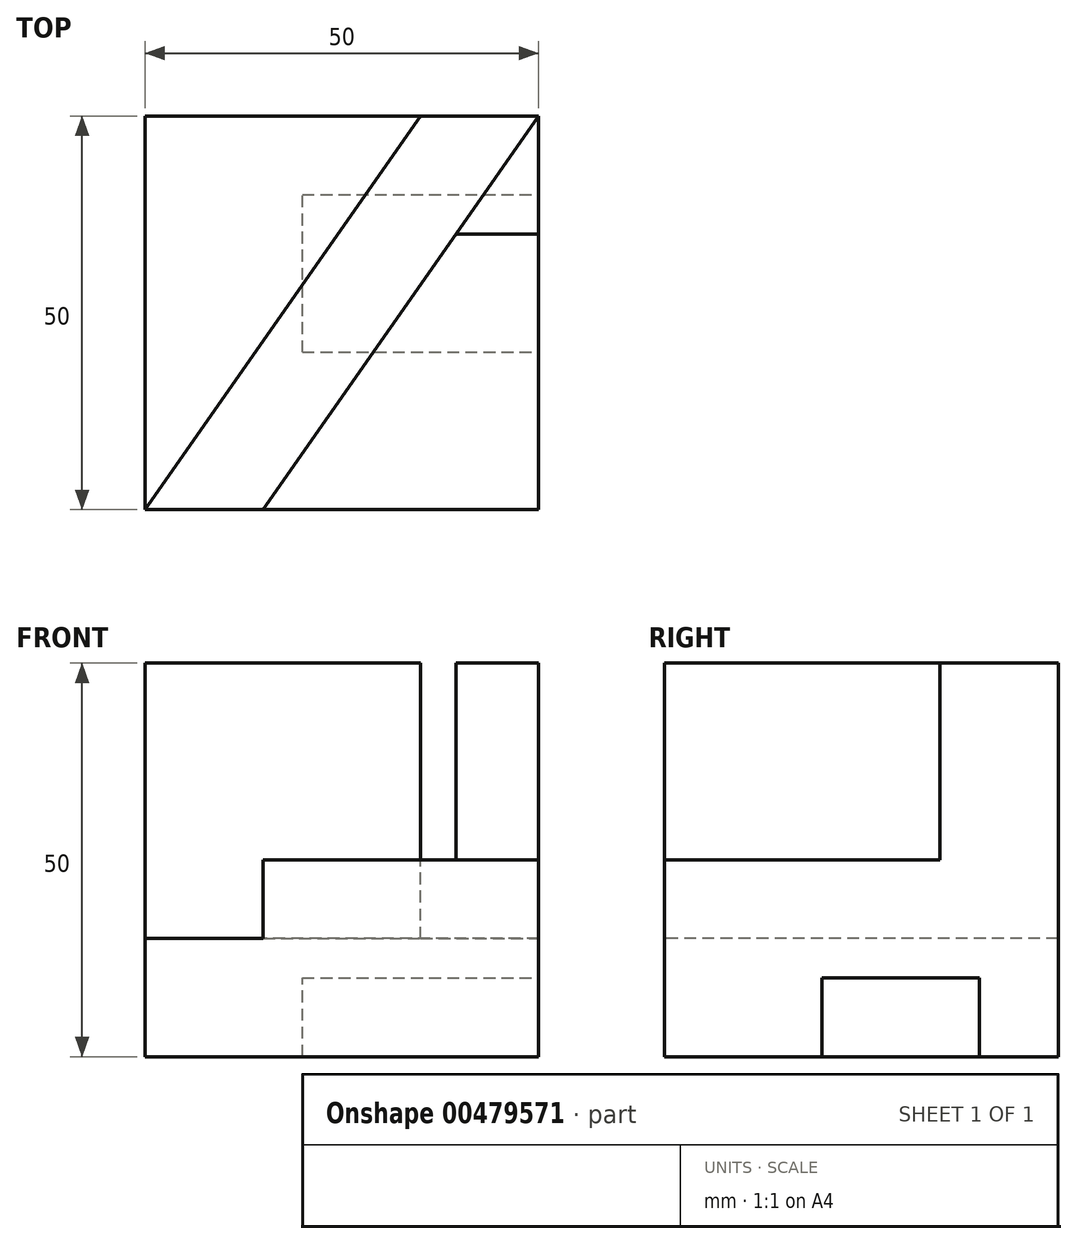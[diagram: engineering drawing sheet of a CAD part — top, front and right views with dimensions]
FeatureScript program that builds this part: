
annotation { "Feature Type Name" : "Feature", "Feature Type Description" : "" }
export const myFeature = defineFeature(function(context is Context, id is Id, definition is map)
    precondition{}
    {
        {
            var Q0;
            Q0=qCreatedBy(makeId("Top.planeOp"),FACE);
            var sketch = newSketch(context, id + "F0", { "sketchPlane" : qUnion([Q0])});
            skLineSegment(sketch, "E0.bottom", {"start": v(0, 0) * mm, "end": v(50, 0) * mm});
            skLineSegment(sketch, "E0.top", {"start": v(0, 50) * mm, "end": v(50, 50) * mm});
            skLineSegment(sketch, "E0.left", {"start": v(0, 0) * mm, "end": v(0, 50) * mm});
            skLineSegment(sketch, "E0.right", {"start": v(50, 0) * mm, "end": v(50, 50) * mm});
            skSolve(sketch);
        }
        {
            var Q0;
            Q0 = qSketchRegion(id + "F0", true);
            extrude(context, id + "F1", {"entities" : qUnion([Q0]), "depth" : 50 * mm});
        }
        {
            var Q0;
            Q0=makeQuery(id+"F1.opExtrude","CAP_FACE",FACE,{"disambiguationData":[OSD([sQuery(id+"F0.wireOp",EDGE,"E0.bottom"),sQuery(id+"F0.wireOp",EDGE,"E0.top"),sQuery(id+"F0.wireOp",EDGE,"E0.left"),sQuery(id+"F0.wireOp",EDGE,"E0.right")])],"isStart":false});
            var sketch = newSketch(context, id + "F2", { "sketchPlane" : qUnion([Q0])});
            skLineSegment(sketch, "E1", {"start": v(50, 50) * mm, "end": v(15, 0) * mm});
            skLineSegment(sketch, "E2", {"start": v(0, 0) * mm, "end": v(35, 50) * mm});
            skSolve(sketch);
        }
        {
            var Q0;
            Q0 = qSketchRegion(id + "F2", true);
            var Q1;
            {var subQ0=sQuery(id+"F2.wireOp",EDGE,"E1");Q1=makeQuery(id+"F2.imprint","IMPRINT",FACE,{"disambiguationData":[TD([[makeQuery(id+"F2.imprint","IMPRINT",EDGE,{"derivedFrom":subQ0}),-1.0]])]});}
            extrude(context, id + "F3", {"entities" : qUnion([Q0, Q1]), "operationType" : NewBodyOperationType.REMOVE, "oppositeDirection" : true, "depth" : 35 * mm});
        }
        {
            var Q0;
            Q0=makeQuery(id+"F1.opExtrude","SWEPT_FACE",FACE,{"disambiguationData":[OSD([sQuery(id+"F0.wireOp",EDGE,"E0.right")])]});
            var sketch = newSketch(context, id + "F4", { "sketchPlane" : qUnion([Q0])});
            skLineSegment(sketch, "E3.bottom", {"start": v(20, 0) * mm, "end": v(40, 0) * mm});
            skLineSegment(sketch, "E3.top", {"start": v(20, 10) * mm, "end": v(40, 10) * mm});
            skLineSegment(sketch, "E3.left", {"start": v(20, 0) * mm, "end": v(20, 10) * mm});
            skLineSegment(sketch, "E3.right", {"start": v(40, 0) * mm, "end": v(40, 10) * mm});
            skSolve(sketch);
        }
        {
            var Q0;
            Q0 = qSketchRegion(id + "F4", true);
            extrude(context, id + "F5", {"entities" : qUnion([Q0]), "operationType" : NewBodyOperationType.REMOVE, "oppositeDirection" : true, "depth" : 30 * mm});
        }
        {
            var Q0;
            {var subQ0=sQuery(id+"F0.wireOp",EDGE,"E0.bottom");var subQ1=sQuery(id+"F0.wireOp",EDGE,"E0.right");Q0=makeQuery(id+"F3.boolean.opBoolean","SPLIT",FACE,{"disambiguationData":[TD([makeQuery(id+"F1.opExtrude","SWEPT_FACE",FACE,{"disambiguationData":[OSD([subQ0])]})])],"derivedFrom":makeQuery(id+"F1.opExtrude","CAP_FACE",FACE,{"disambiguationData":[OSD([subQ0,sQuery(id+"F0.wireOp",EDGE,"E0.top"),sQuery(id+"F0.wireOp",EDGE,"E0.left"),subQ1])],"isStart":false})});}
            var sketch = newSketch(context, id + "F6", { "sketchPlane" : qUnion([Q0])});
            skLineSegment(sketch, "E4", {"start": v(39.5, 35) * mm, "end": v(50, 35) * mm});
            skLineSegment(sketch, "E5", {"start": v(50, 35) * mm, "end": v(50, 0) * mm});
            skLineSegment(sketch, "E6", {"start": v(50, 0) * mm, "end": v(15, 0) * mm});
            skLineSegment(sketch, "E7", {"start": v(15, 0) * mm, "end": v(39.5, 35) * mm});
            skSolve(sketch);
        }
        {
            var Q0;
            Q0 = qSketchRegion(id + "F6", true);
            extrude(context, id + "F7", {"entities" : qUnion([Q0]), "operationType" : NewBodyOperationType.REMOVE, "oppositeDirection" : true, "depth" : 25 * mm});
        }
    });
